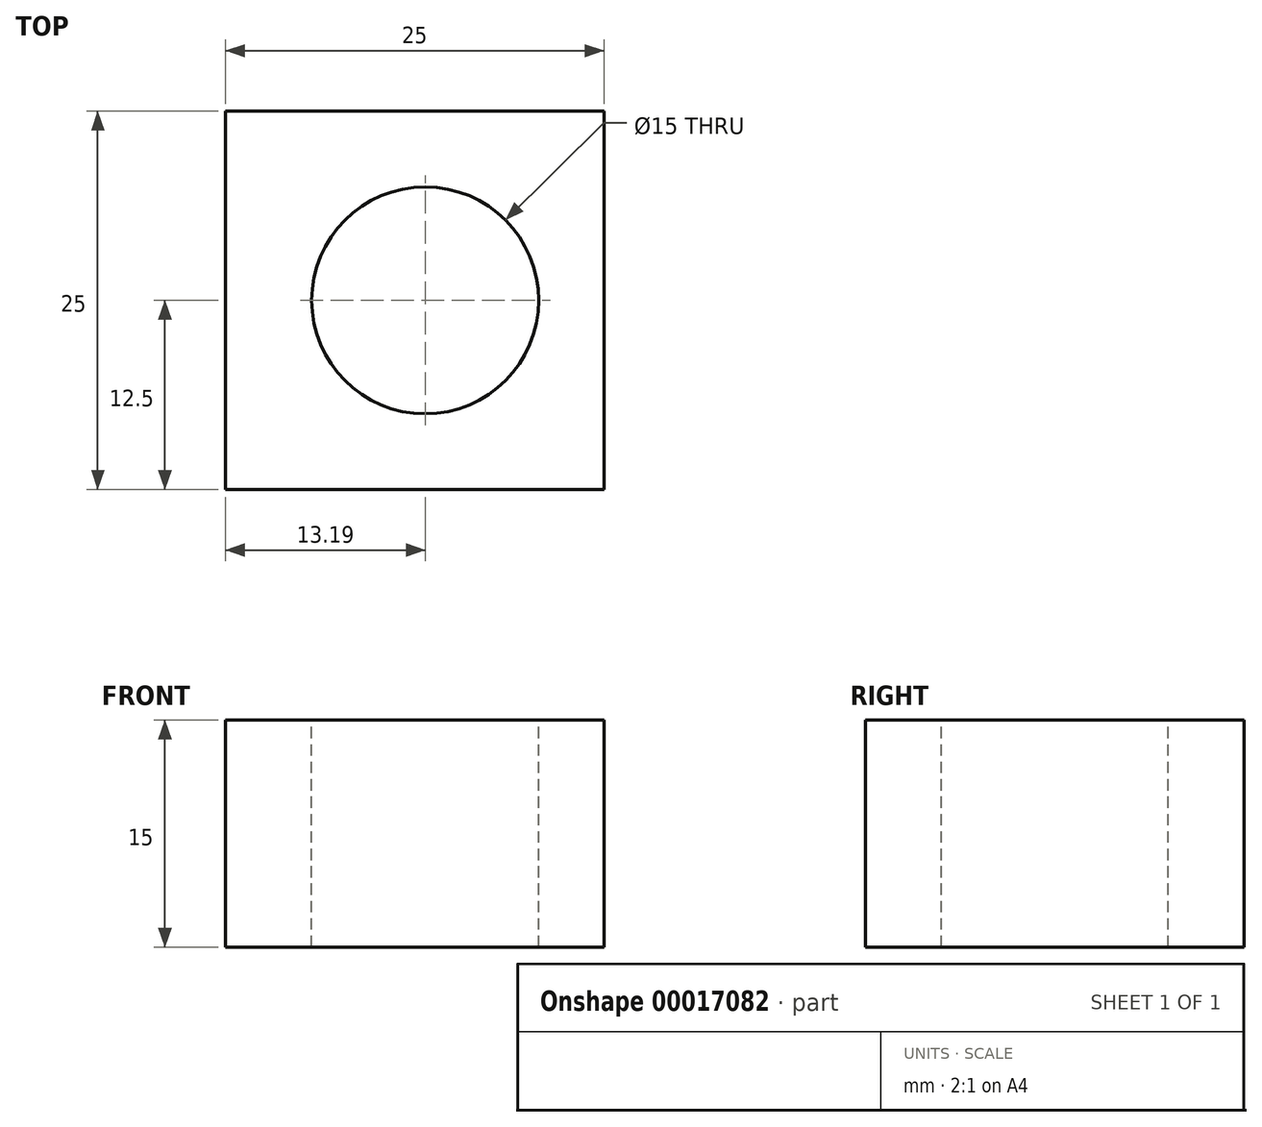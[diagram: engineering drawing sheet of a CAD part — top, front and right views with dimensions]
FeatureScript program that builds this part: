
annotation { "Feature Type Name" : "Feature", "Feature Type Description" : "" }
export const myFeature = defineFeature(function(context is Context, id is Id, definition is map)
    precondition{}
    {
        {
            var Q0;
            Q0=qCreatedBy(makeId("Front.planeOp"),FACE);
            var sketch = newSketch(context, id + "F0", { "sketchPlane" : qUnion([Q0])});
            skLineSegment(sketch, "E0.bottom", {"start": v(-13.19, 2.97) * mm, "end": v(11.81, 2.97) * mm});
            skLineSegment(sketch, "E0.top", {"start": v(-13.19, -12.03) * mm, "end": v(11.81, -12.03) * mm});
            skLineSegment(sketch, "E0.left", {"start": v(-13.19, 2.97) * mm, "end": v(-13.19, -12.03) * mm});
            skLineSegment(sketch, "E0.right", {"start": v(11.81, 2.97) * mm, "end": v(11.81, -12.03) * mm});
            skSolve(sketch);
        }
        {
            var Q0;
            Q0 = qSketchRegion(id + "F0", true);
            extrude(context, id + "F1", {"entities" : qUnion([Q0]), "depth" : 25 * mm});
        }
        {
            var Q0;
            Q0=makeQuery(id+"F1.opExtrude","SWEPT_FACE",FACE,{"disambiguationData":[OSD([sQuery(id+"F0.wireOp",EDGE,"E0.bottom")])]});
            var sketch = newSketch(context, id + "F2", { "sketchPlane" : qUnion([Q0])});
            skCircle(sketch, "E1", {"center": v(0, -12.5) * mm, "radius": 7.5 * mm});
            skSolve(sketch);
        }
        {
            var Q0;
            Q0=makeQuery(id+"F2.imprint","IMPRINT",FACE,{"disambiguationData":[TD([[makeQuery(id+"F2.imprint","IMPRINT",EDGE,{"derivedFrom":sQuery(id+"F2.wireOp",EDGE,"E1")}),1.0]])]});
            extrude(context, id + "F3", {"entities" : qUnion([Q0]), "operationType" : NewBodyOperationType.REMOVE, "endBound" : BoundingType.THROUGH_ALL, "oppositeDirection" : true, "depth" : 25 * mm});
        }
    });
